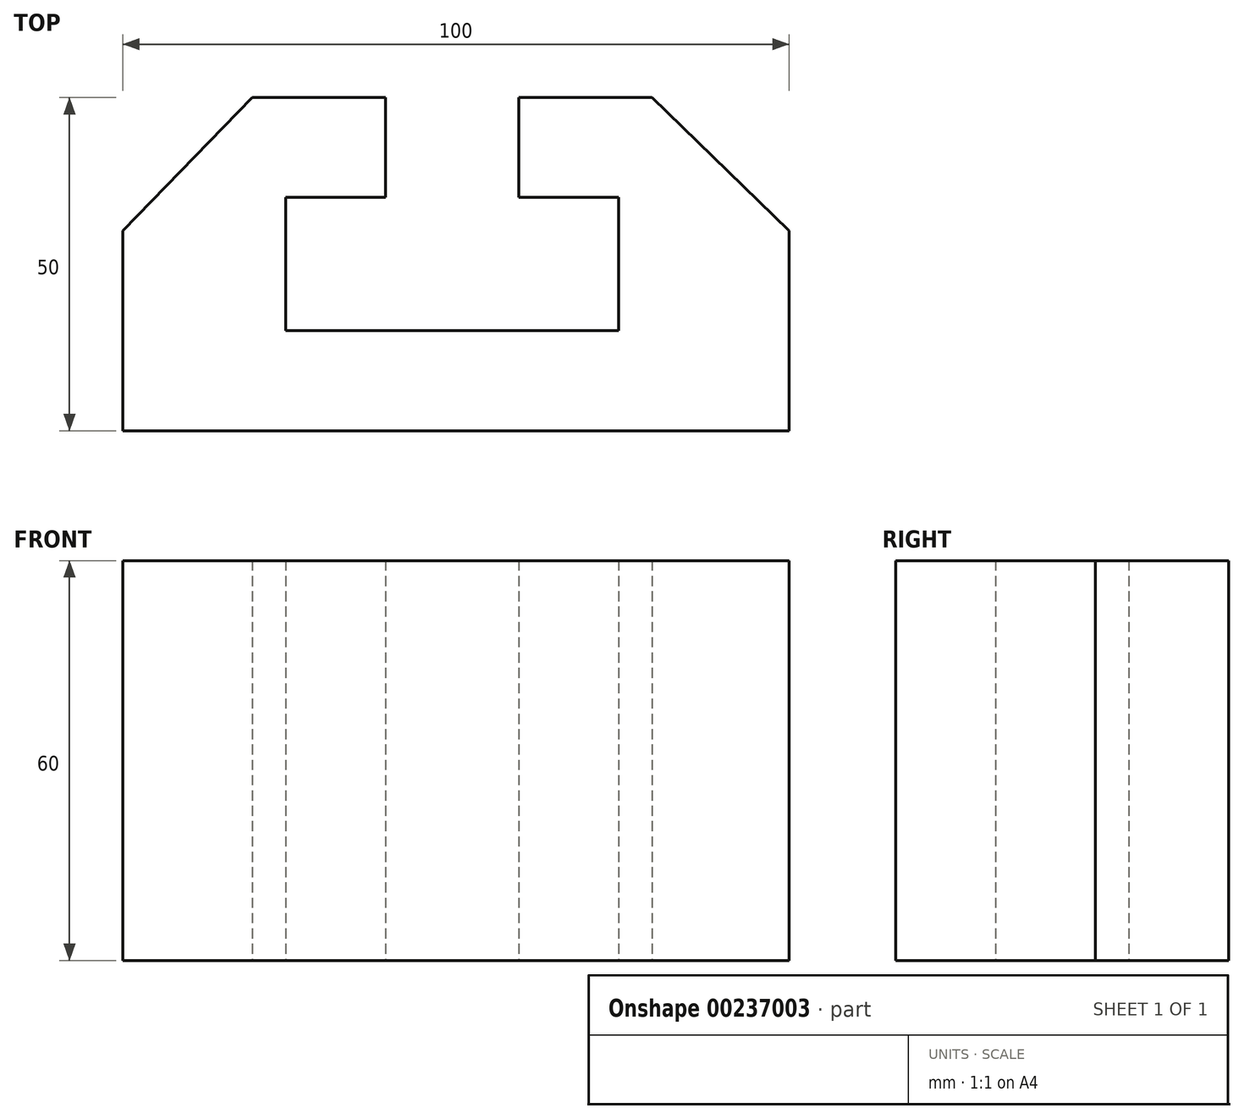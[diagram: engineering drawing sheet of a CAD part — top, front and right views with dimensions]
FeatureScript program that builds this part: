
annotation { "Feature Type Name" : "Feature", "Feature Type Description" : "" }
export const myFeature = defineFeature(function(context is Context, id is Id, definition is map)
    precondition{}
    {
        {
            var Q0;
            Q0=qCreatedBy(makeId("Top.planeOp"),FACE);
            var sketch = newSketch(context, id + "F0", { "sketchPlane" : qUnion([Q0])});
            skLineSegment(sketch, "E0", {"start": v(-65.65, -35) * mm, "end": v(34.35, -35) * mm});
            skLineSegment(sketch, "E1", {"start": v(34.35, -35) * mm, "end": v(34.35, -5) * mm});
            skLineSegment(sketch, "E2", {"start": v(34.35, -5) * mm, "end": v(13.77, 15) * mm});
            skLineSegment(sketch, "E3", {"start": v(13.77, 15) * mm, "end": v(-6.23, 15) * mm});
            skLineSegment(sketch, "E4", {"start": v(-6.23, 15) * mm, "end": v(-6.23, 0) * mm});
            skLineSegment(sketch, "E5", {"start": v(-26.23, 0) * mm, "end": v(-26.23, 15) * mm});
            skLineSegment(sketch, "E6", {"start": v(-26.23, 15) * mm, "end": v(-46.23, 15) * mm});
            skLineSegment(sketch, "E7", {"start": v(-46.23, 15) * mm, "end": v(-65.65, -5) * mm});
            skLineSegment(sketch, "E8", {"start": v(-65.65, -5) * mm, "end": v(-65.65, -35) * mm});
            skLineSegment(sketch, "E9", {"start": v(-6.23, 0) * mm, "end": v(8.77, 0) * mm});
            skLineSegment(sketch, "E10", {"start": v(8.77, 0) * mm, "end": v(8.77, -20) * mm});
            skLineSegment(sketch, "E11", {"start": v(8.77, -20) * mm, "end": v(-41.23, -20) * mm});
            skLineSegment(sketch, "E12", {"start": v(-41.23, -20) * mm, "end": v(-41.23, 0) * mm});
            skLineSegment(sketch, "E13", {"start": v(-41.23, 0) * mm, "end": v(-26.23, 0) * mm});
            skSolve(sketch);
        }
        {
            var Q0;
            Q0=makeQuery(id+"F0.imprint","IMPRINT",FACE,{"disambiguationData":[TD([[makeQuery(id+"F0.imprint","IMPRINT",EDGE,{"derivedFrom":sQuery(id+"F0.wireOp",EDGE,"E0")}),1.0]])]});
            extrude(context, id + "F1", {"entities" : qUnion([Q0]), "depth" : 60 * mm});
        }
    });
